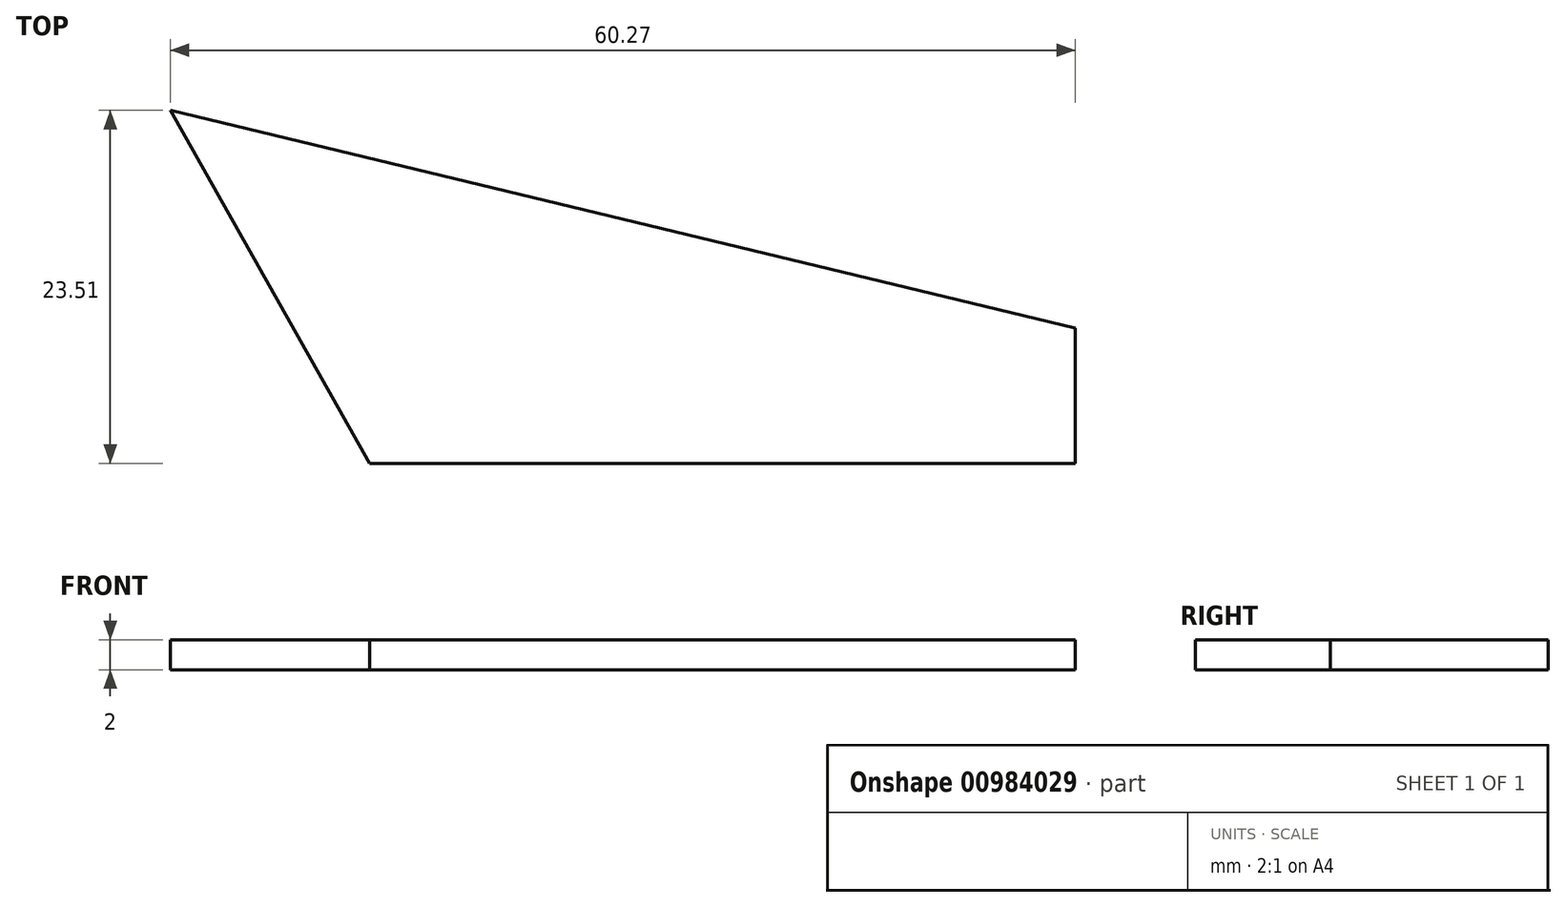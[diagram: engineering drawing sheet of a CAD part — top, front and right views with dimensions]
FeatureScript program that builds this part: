
annotation { "Feature Type Name" : "Feature", "Feature Type Description" : "" }
export const myFeature = defineFeature(function(context is Context, id is Id, definition is map)
    precondition{}
    {
        {
            var Q0;
            Q0=qCreatedBy(makeId("Top.planeOp"),FACE);
            var sketch = newSketch(context, id + "F0", { "sketchPlane" : qUnion([Q0])});
            skLineSegment(sketch, "E0", {"start": v(29.24, 5.95) * mm, "end": v(29.24, -3.05) * mm});
            skLineSegment(sketch, "E1", {"start": v(29.24, -3.05) * mm, "end": v(-17.76, -3.05) * mm});
            skLineSegment(sketch, "E2", {"start": v(-17.76, -3.05) * mm, "end": v(-31.03, 20.46) * mm});
            skLineSegment(sketch, "E3", {"start": v(-31.03, 20.46) * mm, "end": v(29.24, 5.95) * mm});
            skSolve(sketch);
        }
        {
            var Q0;
            Q0=makeQuery(id+"F0.imprint","IMPRINT",FACE,{"disambiguationData":[TD([[makeQuery(id+"F0.imprint","IMPRINT",EDGE,{"derivedFrom":sQuery(id+"F0.wireOp",EDGE,"E0")}),-1.0]])]});
            extrude(context, id + "F1", {"entities" : qUnion([Q0]), "depth" : 2 * mm, "offsetDistance" : 25.4 * mm});
        }
    });
